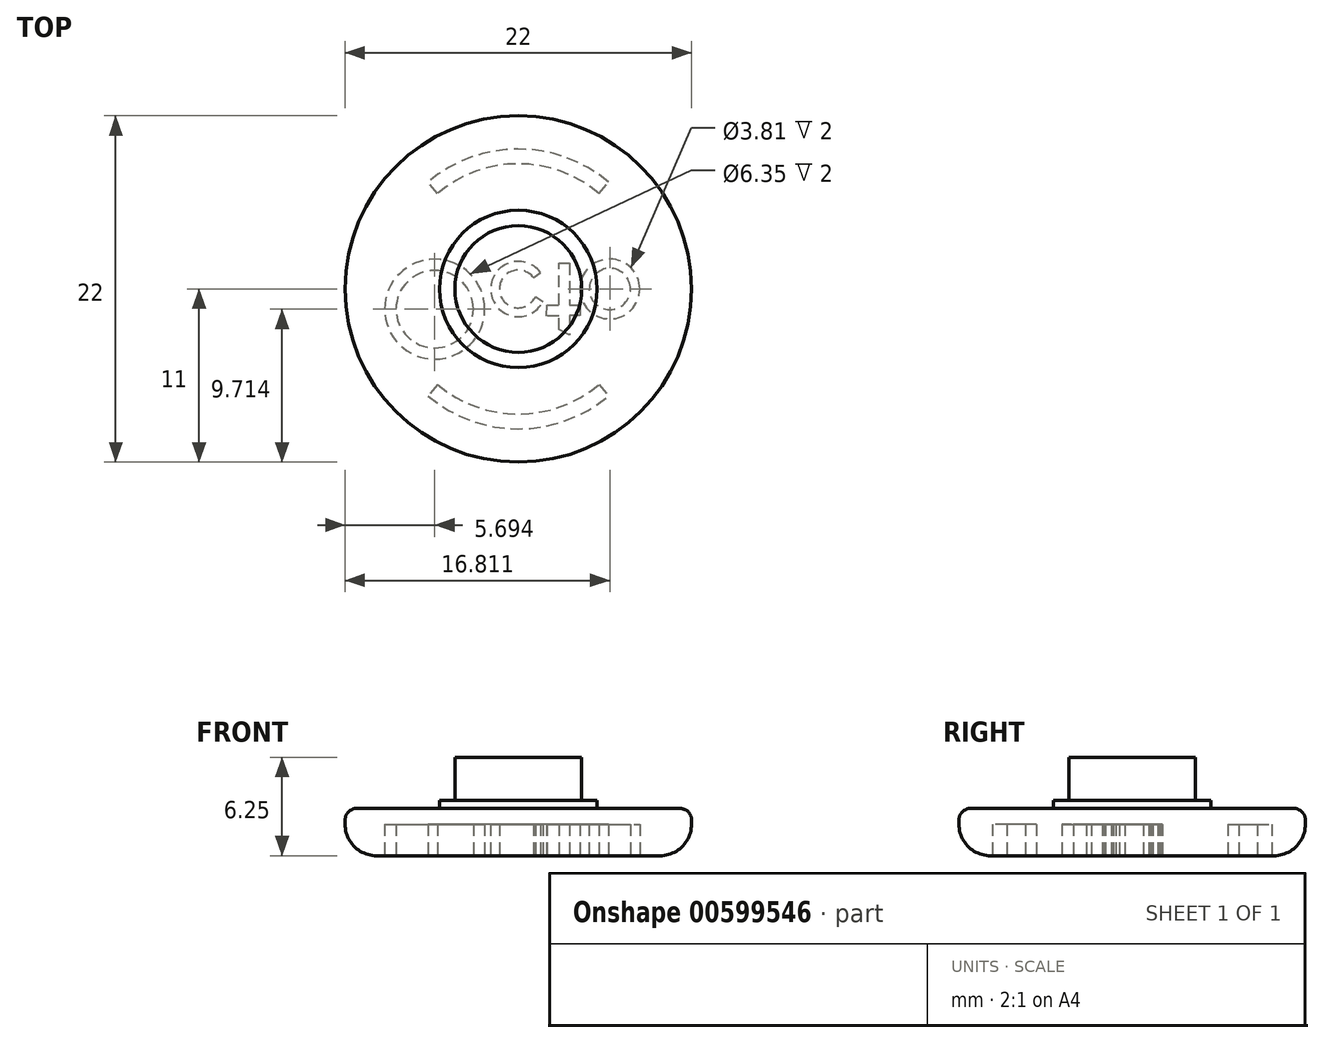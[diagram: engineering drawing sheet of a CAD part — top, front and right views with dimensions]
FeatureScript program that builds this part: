
annotation { "Feature Type Name" : "Feature", "Feature Type Description" : "" }
export const myFeature = defineFeature(function(context is Context, id is Id, definition is map)
    precondition{}
    {
        {
            var Q0;
            Q0=qCreatedBy(makeId("Top.planeOp"),FACE);
            var sketch = newSketch(context, id + "F0", { "sketchPlane" : qUnion([Q0])});
            skCircle(sketch, "E0", {"center": v(0, 0) * mm, "radius": 11 * mm});
            skSolve(sketch);
        }
        {
            var Q0;
            Q0=qSketchRegion(id+"F0",true);
            extrude(context, id + "F1", {"entities" : qUnion([Q0]), "depth" : 3 * mm, "offsetDistance" : 25 * mm});
        }
        {
            var Q0;
            Q0=makeQuery(id+"F1.opExtrude","CAP_EDGE",EDGE,{"disambiguationData":[OSD([sQuery(id+"F0.wireOp",EDGE,"E0")])],"isStart":true});
            fillet(context, id + "F2", {"entities" : qUnion([Q0]), "radius" : 2 * mm, "tangentPropagation" : true, "allowEdgeOverflow" : false});
        }
        {
            var Q0;
            Q0=makeQuery(id+"F1.opExtrude","CAP_FACE",FACE,{"disambiguationData":[OSD([sQuery(id+"F0.wireOp",EDGE,"E0")])],"isStart":false});
            var sketch = newSketch(context, id + "F3", { "sketchPlane" : qUnion([Q0])});
            skCircle(sketch, "E1", {"center": v(0, 0) * mm, "radius": 5 * mm});
            skCircle(sketch, "E2", {"center": v(0, 0) * mm, "radius": 4.03 * mm});
            skSolve(sketch);
        }
        {
            var Q0;
            Q0=makeQuery(id+"F3.imprint","IMPRINT",FACE,{"disambiguationData":[TD([[makeQuery(id+"F3.imprint","IMPRINT",EDGE,{"derivedFrom":sQuery(id+"F3.wireOp",EDGE,"E1")}),1.0]])]});
            extrude(context, id + "F4", {"entities" : qUnion([Q0]), "operationType" : NewBodyOperationType.ADD, "depth" : 0.5 * mm, "offsetDistance" : 25 * mm});
        }
        {
            var Q0;
            Q0=makeQuery(id+"F4.boolean.opBoolean","SPLIT",FACE,{"disambiguationData":[TD([makeQuery(id+"F4.opExtrude","SWEPT_FACE",FACE,{"disambiguationData":[OSD([sQuery(id+"F3.wireOp",EDGE,"E2")])]})])],"derivedFrom":makeQuery(id+"F1.opExtrude","CAP_FACE",FACE,{"disambiguationData":[OSD([sQuery(id+"F0.wireOp",EDGE,"E0")])],"isStart":false})});
            extrude(context, id + "F5", {"entities" : qUnion([Q0]), "operationType" : NewBodyOperationType.ADD, "depth" : 3.25 * mm, "offsetDistance" : 25 * mm});
        }
        {
            var Q0;
            Q0=makeQuery(id+"F1.opExtrude","CAP_FACE",FACE,{"disambiguationData":[OSD([sQuery(id+"F0.wireOp",EDGE,"E0")])],"isStart":true});
            var sketch = newSketch(context, id + "F6", { "sketchPlane" : qUnion([Q0])});
            skCircle(sketch, "E3", {"center": v(-5.3, 1.29) * mm, "radius": 3.18 * mm});
            skCircle(sketch, "E4", {"center": v(-5.3, 1.29) * mm, "radius": 2.46 * mm});
            skArc(sketch, "E5", {"start": v(1.1, 0.47) * mm, "mid": v(-1.2, 0.14) * mm, "end": v(0.96, -0.72) * mm});
            skArc(sketch, "E6", {"start": v(1.56, 0.8) * mm, "mid": v(-1.75, 0.14) * mm, "end": v(1.4, -1.05) * mm});
            skLineSegment(sketch, "E7", {"start": v(1.8, 1.7) * mm, "end": v(1.82, 1.03) * mm});
            skLineSegment(sketch, "E8", {"start": v(1.82, 1.03) * mm, "end": v(2.6, 1.03) * mm});
            skLineSegment(sketch, "E9", {"start": v(2.6, 1.03) * mm, "end": v(2.6, -1.64) * mm});
            skLineSegment(sketch, "E10", {"start": v(2.6, -1.64) * mm, "end": v(3.26, -1.64) * mm});
            skLineSegment(sketch, "E11", {"start": v(3.26, -1.64) * mm, "end": v(3.26, 1.04) * mm});
            skLineSegment(sketch, "E12", {"start": v(3.26, 1.04) * mm, "end": v(3.91, 1.04) * mm});
            skLineSegment(sketch, "E13", {"start": v(3.91, 1.04) * mm, "end": v(3.91, 1.69) * mm});
            skLineSegment(sketch, "E14", {"start": v(3.91, 1.69) * mm, "end": v(3.27, 1.69) * mm});
            skLineSegment(sketch, "E15", {"start": v(3.27, 1.69) * mm, "end": v(3.27, 2.92) * mm});
            skLineSegment(sketch, "E16", {"start": v(3.27, 2.92) * mm, "end": v(2.6, 2.6) * mm});
            skLineSegment(sketch, "E17", {"start": v(2.6, 2.6) * mm, "end": v(2.6, 1.72) * mm});
            skLineSegment(sketch, "E18", {"start": v(2.6, 1.72) * mm, "end": v(1.8, 1.7) * mm});
            skLineSegment(sketch, "E19", {"start": v(1.1, 0.47) * mm, "end": v(1.56, 0.8) * mm});
            skLineSegment(sketch, "E20", {"start": v(0.96, -0.72) * mm, "end": v(1.4, -1.05) * mm});
            skCircle(sketch, "E21", {"center": v(5.81, 0) * mm, "radius": 1.3 * mm});
            skCircle(sketch, "E22", {"center": v(5.81, 0) * mm, "radius": 1.9 * mm});
            skArc(sketch, "E23", {"start": v(5.73, 6.8) * mm, "mid": v(0, 8.89) * mm, "end": v(-5.73, 6.8) * mm});
            skArc(sketch, "E24", {"start": v(5.13, 6.07) * mm, "mid": v(0, 7.95) * mm, "end": v(-5.13, 6.07) * mm});
            skLineSegment(sketch, "E25", {"start": v(-5.13, -6.07) * mm, "end": v(-5.73, -6.8) * mm});
            skLineSegment(sketch, "E26.MirrorCS", {"start": v(-5.13, 6.07) * mm, "end": v(-5.73, 6.8) * mm});
            skLineSegment(sketch, "E27.MirrorCS", {"start": v(5.13, 6.07) * mm, "end": v(5.73, 6.8) * mm});
            skLineSegment(sketch, "E28.MirrorCS", {"start": v(5.13, -6.07) * mm, "end": v(5.73, -6.8) * mm});
            skPoint(sketch, "E29.orphan", {"position": v(1.1, 0) * mm});
            skArc(sketch, "E30.trimOffspring", {"start": v(-5.13, -6.07) * mm, "mid": v(0, -7.95) * mm, "end": v(5.13, -6.07) * mm});
            skArc(sketch, "E31.trimOffspring", {"start": v(-5.73, -6.8) * mm, "mid": v(0, -8.89) * mm, "end": v(5.73, -6.8) * mm});
            skSolve(sketch);
        }
        {
            var Q0;
            Q0=qSketchRegion(id+"F6",true);
            var Q1;
            Q1=qConstructionFilter(qBodyType(qCreatedBy(id+"F6",EDGE),BodyType.WIRE),ConstructionObject.NO);
            extrude(context, id + "F7", {"entities" : qUnion([Q0]), "operationType" : NewBodyOperationType.REMOVE, "surfaceEntities" : qUnion([Q1]), "oppositeDirection" : true, "depth" : 2 * mm, "offsetDistance" : 25 * mm});
        }
        {
            var Q0;
            Q0=makeQuery(id+"F1.opExtrude","CAP_EDGE",EDGE,{"disambiguationData":[OSD([sQuery(id+"F0.wireOp",EDGE,"E0")])],"isStart":false});
            fillet(context, id + "F8", {"entities" : qUnion([Q0]), "radius" : 0.72 * mm, "tangentPropagation" : true, "allowEdgeOverflow" : false});
        }
    });
